# Revit family: FU_Table_Sandler_Chicago 1 9
name_source: partatom
category: Furniture
units: mm (PartAtom-declared; Revit-internal decimal feet)

## family parameters
Always vertical = Yes
Cut with Voids When Loaded = No
OmniClass Number = 23.40.20.00
OmniClass Title = General Furniture and Specialties
Room Calculation Point = No
Shared = No
Work Plane-Based = No

## types (3) — shared parameters
Assembly Code = E2020
Description = *Please enter mtrl description here for use in mto*
Diameter = 540 mm
Frame Material = Metal - Chrome - Polished
Height = 570 mm
Keynote = 46.B
Manufacturer = LAMMHULTS
Model = CHICAGO
URL = www.lammhults.se
zero-valued in all types: Default Elevation

## per-type parameters (varying)
| type | Shelves Material | Top Shelve Material |
| Glass | Glass-Frosted | Glass-Frosted |
| Laminate | Laminate - High Pressure - White grey | Laminate - High Pressure - White grey |
| Leather | Leather - Rustical - Brown | Leather - Rustical - Brown |

## geometry (parser evidence)
native form markers: Blend x8, Sweep x2
no freeform markers — native parametric forms only
